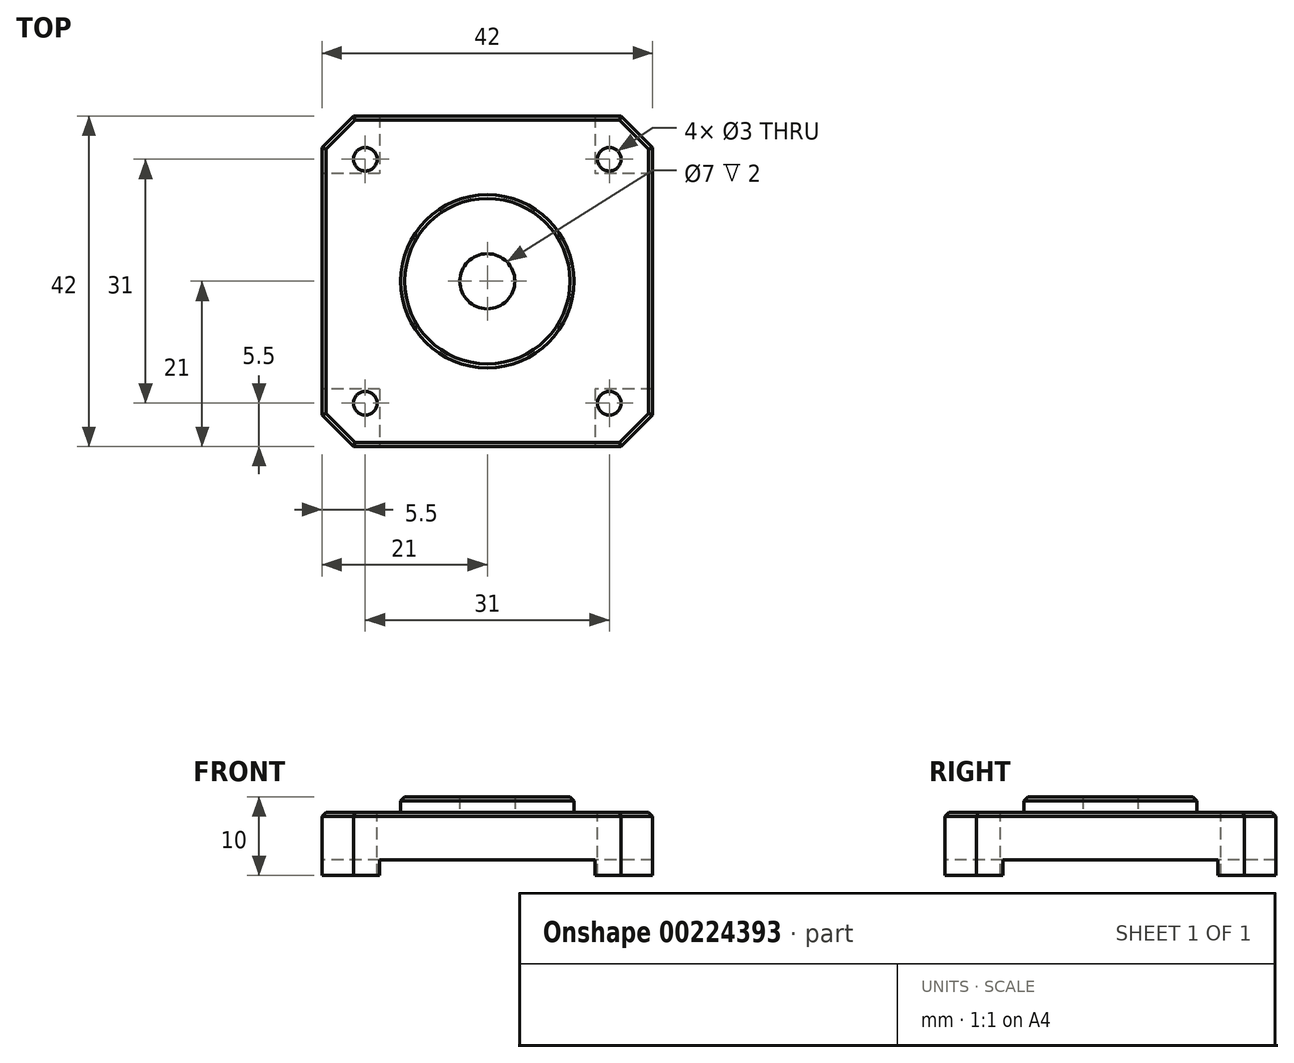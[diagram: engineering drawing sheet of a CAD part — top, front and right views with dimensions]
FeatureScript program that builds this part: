
annotation { "Feature Type Name" : "Feature", "Feature Type Description" : "" }
export const myFeature = defineFeature(function(context is Context, id is Id, definition is map)
    precondition{}
    {
        {
            var Q0;
            Q0=qCreatedBy(makeId("Top.planeOp"),FACE);
            var sketch = newSketch(context, id + "F0", { "sketchPlane" : qUnion([Q0])});
            skLineSegment(sketch, "E0.bottom", {"start": v(21, 21) * mm, "end": v(-21, 21) * mm});
            skLineSegment(sketch, "E0.top", {"start": v(21, -21) * mm, "end": v(-21, -21) * mm});
            skLineSegment(sketch, "E0.left", {"start": v(21, 21) * mm, "end": v(21, -21) * mm});
            skLineSegment(sketch, "E0.right", {"start": v(-21, 21) * mm, "end": v(-21, -21) * mm});
            skPoint(sketch, "E0.middle", {"position": v(0, 0) * mm});
            skCircle(sketch, "E1", {"center": v(0, 0) * mm, "radius": 11 * mm});
            skLineSegment(sketch, "E2.bottom", {"start": v(15.5, 15.5) * mm, "end": v(-15.5, 15.5) * mm, "construction": true});
            skLineSegment(sketch, "E2.top", {"start": v(15.5, -15.5) * mm, "end": v(-15.5, -15.5) * mm, "construction": true});
            skLineSegment(sketch, "E2.left", {"start": v(15.5, 15.5) * mm, "end": v(15.5, -15.5) * mm, "construction": true});
            skLineSegment(sketch, "E2.right", {"start": v(-15.5, 15.5) * mm, "end": v(-15.5, -15.5) * mm, "construction": true});
            skCircle(sketch, "E3", {"center": v(0, 0) * mm, "radius": 3.5 * mm});
            skSolve(sketch);
        }
        {
            var Q0;
            Q0=makeQuery(id+"F0.imprint","IMPRINT",FACE,{"disambiguationData":[TD([[makeQuery(id+"F0.imprint","IMPRINT",EDGE,{"derivedFrom":sQuery(id+"F0.wireOp",EDGE,"E0.bottom")}),1.0]])]});
            var Q1;
            Q1=makeQuery(id+"F0.imprint","IMPRINT",FACE,{"disambiguationData":[TD([[makeQuery(id+"F0.imprint","IMPRINT",EDGE,{"derivedFrom":sQuery(id+"F0.wireOp",EDGE,"E1")}),1.0]])]});
            var Q2;
            Q2=makeQuery(id+"F0.imprint","IMPRINT",FACE,{"disambiguationData":[TD([[makeQuery(id+"F0.imprint","IMPRINT",EDGE,{"derivedFrom":sQuery(id+"F0.wireOp",EDGE,"E3")}),1.0]])]});
            extrude(context, id + "F1", {"entities" : qUnion([Q0, Q1, Q2]), "oppositeDirection" : true, "depth" : 8 * mm});
        }
        {
            var Q0;
            Q0=makeQuery(id+"F0.imprint","IMPRINT",FACE,{"disambiguationData":[TD([[makeQuery(id+"F0.imprint","IMPRINT",EDGE,{"derivedFrom":sQuery(id+"F0.wireOp",EDGE,"E1")}),1.0]])]});
            extrude(context, id + "F2", {"entities" : qUnion([Q0]), "operationType" : NewBodyOperationType.ADD, "depth" : 2 * mm});
        }
        {
            var Q0;
            Q0=sQuery(id+"F0.wireOp",VERTEX,"E2.left.start");
            var Q1;
            Q1=sQuery(id+"F0.wireOp",VERTEX,"E2.left.end");
            var Q2;
            Q2=sQuery(id+"F0.wireOp",VERTEX,"E2.right.end");
            var Q3;
            Q3=sQuery(id+"F0.wireOp",VERTEX,"E2.right.start");
            var Q4;
            Q4=makeQuery(id+"F1.opExtrude","SWEPT_BODY",BODY,{"disambiguationData":[OSD([sQuery(id+"F0.wireOp",EDGE,"E0.bottom"),sQuery(id+"F0.wireOp",EDGE,"E0.top"),sQuery(id+"F0.wireOp",EDGE,"E0.left"),sQuery(id+"F0.wireOp",EDGE,"E0.right")])]});
            hole(context, id + "F3", {"style" : HoleStyle.SIMPLE, "endStyle" : HoleEndStyle.THROUGH, "holeDiameter" : 3 * mm, "locations" : qUnion([Q0, Q1, Q2, Q3]), "scope" : qUnion([Q4]), "isTappedThrough" : true});
        }
        {
            var Q0;
            Q0=makeQuery(id+"F1.opExtrude","SWEPT_FACE",FACE,{"disambiguationData":[OSD([sQuery(id+"F0.wireOp",EDGE,"E0.top")])]});
            var sketch = newSketch(context, id + "F4", { "sketchPlane" : qUnion([Q0])});
            skLineSegment(sketch, "E4", {"start": v(-13.68, -8) * mm, "end": v(-13.68, -6) * mm});
            skLineSegment(sketch, "E5", {"start": v(-13.68, -6) * mm, "end": v(13.68, -6) * mm});
            skLineSegment(sketch, "E6", {"start": v(13.68, -6) * mm, "end": v(13.68, -8) * mm});
            skPoint(sketch, "E7", {"position": v(0, -6) * mm});
            skSolve(sketch);
        }
        {
            var Q0;
            {var subQ0=sQuery(id+"F4.wireOp",EDGE,"E4");Q0=makeQuery(id+"F4.imprint","IMPRINT",FACE,{"disambiguationData":[TD([[makeQuery(id+"F4.imprint","IMPRINT",EDGE,{"derivedFrom":subQ0}),-1.0]])]});}
            var Q1;
            Q1=makeQuery(id+"F1.opExtrude","SWEPT_FACE",FACE,{"disambiguationData":[OSD([sQuery(id+"F0.wireOp",EDGE,"E0.bottom")])]});
            extrude(context, id + "F5", {"entities" : qUnion([Q0]), "operationType" : NewBodyOperationType.REMOVE, "endBound" : BoundingType.UP_TO_SURFACE, "oppositeDirection" : true, "endBoundEntityFace" : qUnion([Q1]), "depth" : 25 * mm});
        }
        {
            var Q0;
            Q0=makeQuery(id+"F1.opExtrude","SWEPT_FACE",FACE,{"disambiguationData":[OSD([sQuery(id+"F0.wireOp",EDGE,"E0.right")])]});
            var sketch = newSketch(context, id + "F6", { "sketchPlane" : qUnion([Q0])});
            skLineSegment(sketch, "E8", {"start": v(-13.68, -8) * mm, "end": v(-13.68, -6) * mm});
            skLineSegment(sketch, "E9", {"start": v(-13.68, -6) * mm, "end": v(13.68, -6) * mm});
            skLineSegment(sketch, "E10", {"start": v(13.68, -6) * mm, "end": v(13.68, -8) * mm});
            skPoint(sketch, "E11", {"position": v(0, -6) * mm});
            skSolve(sketch);
        }
        {
            var Q0;
            {var subQ0=sQuery(id+"F6.wireOp",EDGE,"E8");Q0=makeQuery(id+"F6.imprint","IMPRINT",FACE,{"disambiguationData":[TD([[makeQuery(id+"F6.imprint","IMPRINT",EDGE,{"derivedFrom":subQ0}),-1.0]])]});}
            var Q1;
            Q1=makeQuery(id+"F1.opExtrude","SWEPT_FACE",FACE,{"disambiguationData":[OSD([sQuery(id+"F0.wireOp",EDGE,"E0.left")])]});
            extrude(context, id + "F7", {"entities" : qUnion([Q0]), "operationType" : NewBodyOperationType.REMOVE, "endBound" : BoundingType.UP_TO_SURFACE, "oppositeDirection" : true, "endBoundEntityFace" : qUnion([Q1]), "depth" : 25 * mm});
        }
        {
            var Q0;
            Q0=makeQuery(id+"F1.opExtrude","SWEPT_EDGE",EDGE,{"disambiguationData":[OSD([sQuery(id+"F0.wireOp",EDGE,"E0.top"),sQuery(id+"F0.wireOp",EDGE,"E0.right")])]});
            var Q1;
            Q1=makeQuery(id+"F1.opExtrude","SWEPT_EDGE",EDGE,{"disambiguationData":[OSD([sQuery(id+"F0.wireOp",EDGE,"E0.bottom"),sQuery(id+"F0.wireOp",EDGE,"E0.right")])]});
            var Q2;
            Q2=makeQuery(id+"F1.opExtrude","SWEPT_EDGE",EDGE,{"disambiguationData":[OSD([sQuery(id+"F0.wireOp",EDGE,"E0.top"),sQuery(id+"F0.wireOp",EDGE,"E0.left")])]});
            var Q3;
            Q3=makeQuery(id+"F1.opExtrude","SWEPT_EDGE",EDGE,{"disambiguationData":[OSD([sQuery(id+"F0.wireOp",EDGE,"E0.bottom"),sQuery(id+"F0.wireOp",EDGE,"E0.left")])]});
            chamfer(context, id + "F8", {"entities" : qUnion([Q0, Q1, Q2, Q3]), "width" : 4 * mm, "tangentPropagation" : true});
        }
        {
            var Q0;
            Q0=makeQuery(id+"F2.opExtrude","CAP_EDGE",EDGE,{"disambiguationData":[OSD([sQuery(id+"F0.wireOp",EDGE,"E1")])],"isStart":false});
            var Q1;
            Q1=makeQuery(id+"F1.opExtrude","CAP_EDGE",EDGE,{"disambiguationData":[OSD([sQuery(id+"F0.wireOp",EDGE,"E0.right")])],"isStart":true});
            var Q2;
            {var subQ0=sQuery(id+"F0.wireOp",EDGE,"E0.right");var subQ1=sQuery(id+"F0.wireOp",EDGE,"E0.left");var subQ2=sQuery(id+"F0.wireOp",EDGE,"E0.top");var subQ3=sQuery(id+"F0.wireOp",EDGE,"E0.bottom");Q2=makeQuery(id+"F8.opChamfer","BLEND_EDGE",EDGE,{"blendedFrom":[makeQuery(id+"F1.opExtrude","SWEPT_EDGE",EDGE,{"disambiguationData":[OSD([subQ2,subQ0])]}),makeQuery(id+"F2.boolean.opBoolean","SPLIT",FACE,{"disambiguationData":[TD([makeQuery(id+"F1.opExtrude","SWEPT_FACE",FACE,{"disambiguationData":[OSD([subQ3])]})])],"derivedFrom":makeQuery(id+"F1.opExtrude","CAP_FACE",FACE,{"disambiguationData":[OSD([subQ3,subQ2,subQ1,subQ0])],"isStart":true})})],"blendedInto":[makeQuery(id+"F2.boolean.opBoolean","SPLIT",FACE,{"disambiguationData":[TD([makeQuery(id+"F1.opExtrude","SWEPT_FACE",FACE,{"disambiguationData":[OSD([subQ3])]})])],"derivedFrom":makeQuery(id+"F1.opExtrude","CAP_FACE",FACE,{"disambiguationData":[OSD([subQ3,subQ2,subQ1,subQ0])],"isStart":true})})]});}
            var Q3;
            Q3=makeQuery(id+"F1.opExtrude","CAP_EDGE",EDGE,{"disambiguationData":[OSD([sQuery(id+"F0.wireOp",EDGE,"E0.top")])],"isStart":true});
            var Q4;
            {var subQ0=sQuery(id+"F0.wireOp",EDGE,"E0.right");var subQ1=sQuery(id+"F0.wireOp",EDGE,"E0.left");var subQ2=sQuery(id+"F0.wireOp",EDGE,"E0.top");var subQ3=sQuery(id+"F0.wireOp",EDGE,"E0.bottom");Q4=makeQuery(id+"F8.opChamfer","BLEND_EDGE",EDGE,{"blendedFrom":[makeQuery(id+"F1.opExtrude","SWEPT_EDGE",EDGE,{"disambiguationData":[OSD([subQ2,subQ1])]}),makeQuery(id+"F2.boolean.opBoolean","SPLIT",FACE,{"disambiguationData":[TD([makeQuery(id+"F1.opExtrude","SWEPT_FACE",FACE,{"disambiguationData":[OSD([subQ3])]})])],"derivedFrom":makeQuery(id+"F1.opExtrude","CAP_FACE",FACE,{"disambiguationData":[OSD([subQ3,subQ2,subQ1,subQ0])],"isStart":true})})],"blendedInto":[makeQuery(id+"F2.boolean.opBoolean","SPLIT",FACE,{"disambiguationData":[TD([makeQuery(id+"F1.opExtrude","SWEPT_FACE",FACE,{"disambiguationData":[OSD([subQ3])]})])],"derivedFrom":makeQuery(id+"F1.opExtrude","CAP_FACE",FACE,{"disambiguationData":[OSD([subQ3,subQ2,subQ1,subQ0])],"isStart":true})})]});}
            var Q5;
            Q5=makeQuery(id+"F1.opExtrude","CAP_EDGE",EDGE,{"disambiguationData":[OSD([sQuery(id+"F0.wireOp",EDGE,"E0.left")])],"isStart":true});
            var Q6;
            {var subQ0=sQuery(id+"F0.wireOp",EDGE,"E0.right");var subQ1=sQuery(id+"F0.wireOp",EDGE,"E0.left");var subQ2=sQuery(id+"F0.wireOp",EDGE,"E0.top");var subQ3=sQuery(id+"F0.wireOp",EDGE,"E0.bottom");Q6=makeQuery(id+"F8.opChamfer","BLEND_EDGE",EDGE,{"blendedFrom":[makeQuery(id+"F1.opExtrude","SWEPT_EDGE",EDGE,{"disambiguationData":[OSD([subQ3,subQ1])]}),makeQuery(id+"F2.boolean.opBoolean","SPLIT",FACE,{"disambiguationData":[TD([makeQuery(id+"F1.opExtrude","SWEPT_FACE",FACE,{"disambiguationData":[OSD([subQ3])]})])],"derivedFrom":makeQuery(id+"F1.opExtrude","CAP_FACE",FACE,{"disambiguationData":[OSD([subQ3,subQ2,subQ1,subQ0])],"isStart":true})})],"blendedInto":[makeQuery(id+"F2.boolean.opBoolean","SPLIT",FACE,{"disambiguationData":[TD([makeQuery(id+"F1.opExtrude","SWEPT_FACE",FACE,{"disambiguationData":[OSD([subQ3])]})])],"derivedFrom":makeQuery(id+"F1.opExtrude","CAP_FACE",FACE,{"disambiguationData":[OSD([subQ3,subQ2,subQ1,subQ0])],"isStart":true})})]});}
            var Q7;
            Q7=makeQuery(id+"F1.opExtrude","CAP_EDGE",EDGE,{"disambiguationData":[OSD([sQuery(id+"F0.wireOp",EDGE,"E0.bottom")])],"isStart":true});
            var Q8;
            {var subQ0=sQuery(id+"F0.wireOp",EDGE,"E0.right");var subQ1=sQuery(id+"F0.wireOp",EDGE,"E0.left");var subQ2=sQuery(id+"F0.wireOp",EDGE,"E0.top");var subQ3=sQuery(id+"F0.wireOp",EDGE,"E0.bottom");Q8=makeQuery(id+"F8.opChamfer","BLEND_EDGE",EDGE,{"blendedFrom":[makeQuery(id+"F1.opExtrude","SWEPT_EDGE",EDGE,{"disambiguationData":[OSD([subQ3,subQ0])]}),makeQuery(id+"F2.boolean.opBoolean","SPLIT",FACE,{"disambiguationData":[TD([makeQuery(id+"F1.opExtrude","SWEPT_FACE",FACE,{"disambiguationData":[OSD([subQ3])]})])],"derivedFrom":makeQuery(id+"F1.opExtrude","CAP_FACE",FACE,{"disambiguationData":[OSD([subQ3,subQ2,subQ1,subQ0])],"isStart":true})})],"blendedInto":[makeQuery(id+"F2.boolean.opBoolean","SPLIT",FACE,{"disambiguationData":[TD([makeQuery(id+"F1.opExtrude","SWEPT_FACE",FACE,{"disambiguationData":[OSD([subQ3])]})])],"derivedFrom":makeQuery(id+"F1.opExtrude","CAP_FACE",FACE,{"disambiguationData":[OSD([subQ3,subQ2,subQ1,subQ0])],"isStart":true})})]});}
            chamfer(context, id + "F9", {"entities" : qUnion([Q0, Q1, Q2, Q3, Q4, Q5, Q6, Q7, Q8]), "width" : 0.5 * mm, "tangentPropagation" : true});
        }
    });
